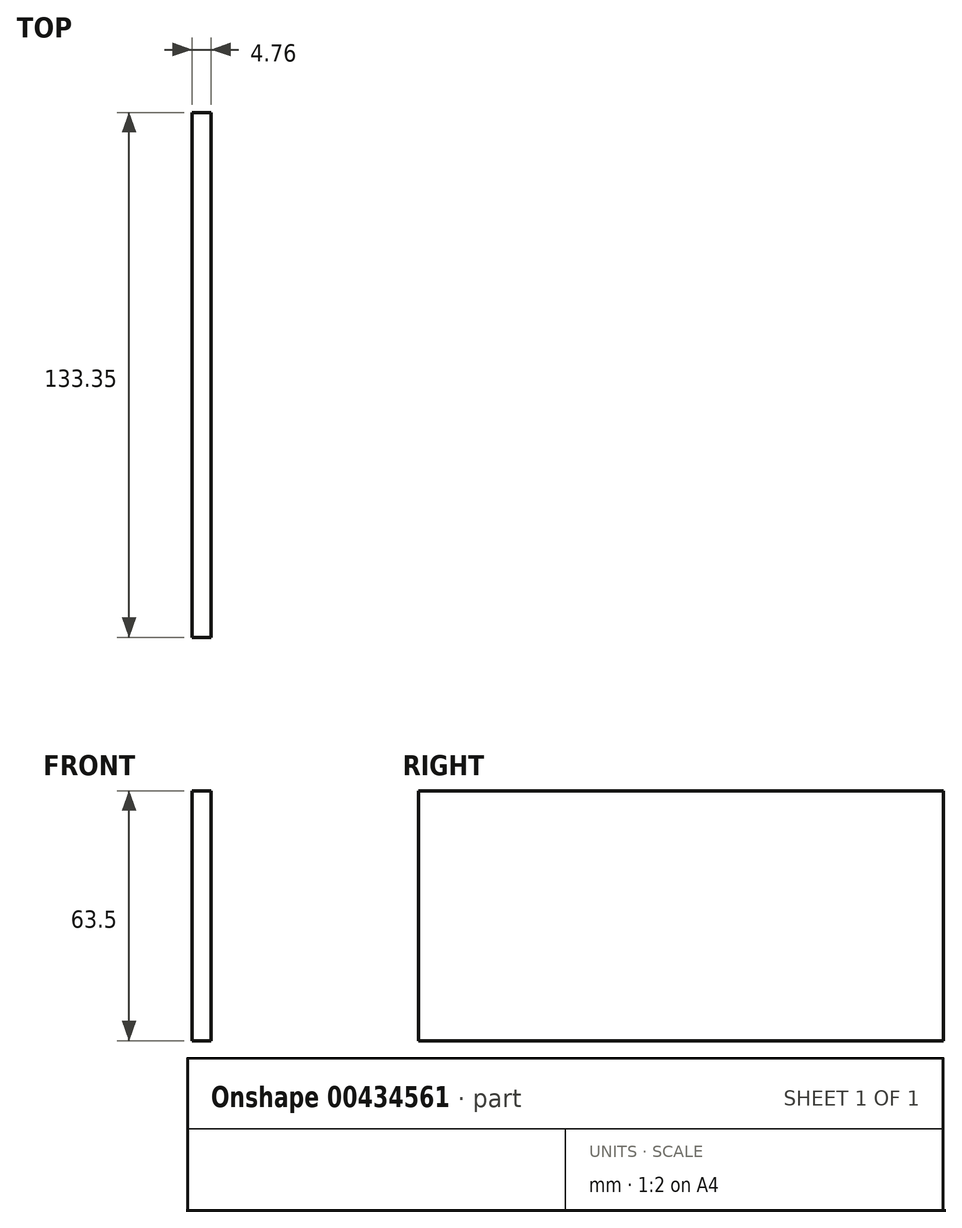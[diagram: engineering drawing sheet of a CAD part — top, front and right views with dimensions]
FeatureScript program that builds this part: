
annotation { "Feature Type Name" : "Feature", "Feature Type Description" : "" }
export const myFeature = defineFeature(function(context is Context, id is Id, definition is map)
    precondition{}
    {
        {
            var Q0;
            Q0=qCreatedBy(makeId("Right.planeOp"),FACE);
            var sketch = newSketch(context, id + "F0", { "sketchPlane" : qUnion([Q0])});
            skLineSegment(sketch, "E0.bottom", {"start": v(-42.9, 39.77) * mm, "end": v(90.45, 39.77) * mm});
            skLineSegment(sketch, "E0.top", {"start": v(-42.9, -23.73) * mm, "end": v(90.45, -23.73) * mm});
            skLineSegment(sketch, "E0.left", {"start": v(-42.9, 39.77) * mm, "end": v(-42.9, -23.73) * mm});
            skLineSegment(sketch, "E0.right", {"start": v(90.45, 39.77) * mm, "end": v(90.45, -23.73) * mm});
            skSolve(sketch);
        }
        {
            var Q0;
            Q0=makeQuery(id+"F0.imprint","IMPRINT",FACE,{"disambiguationData":[TD([[makeQuery(id+"F0.imprint","IMPRINT",EDGE,{"derivedFrom":sQuery(id+"F0.wireOp",EDGE,"E0.bottom")}),-1.0]])]});
            extrude(context, id + "F1", {"entities" : qUnion([Q0]), "depth" : 4.76 * mm});
        }
    });
